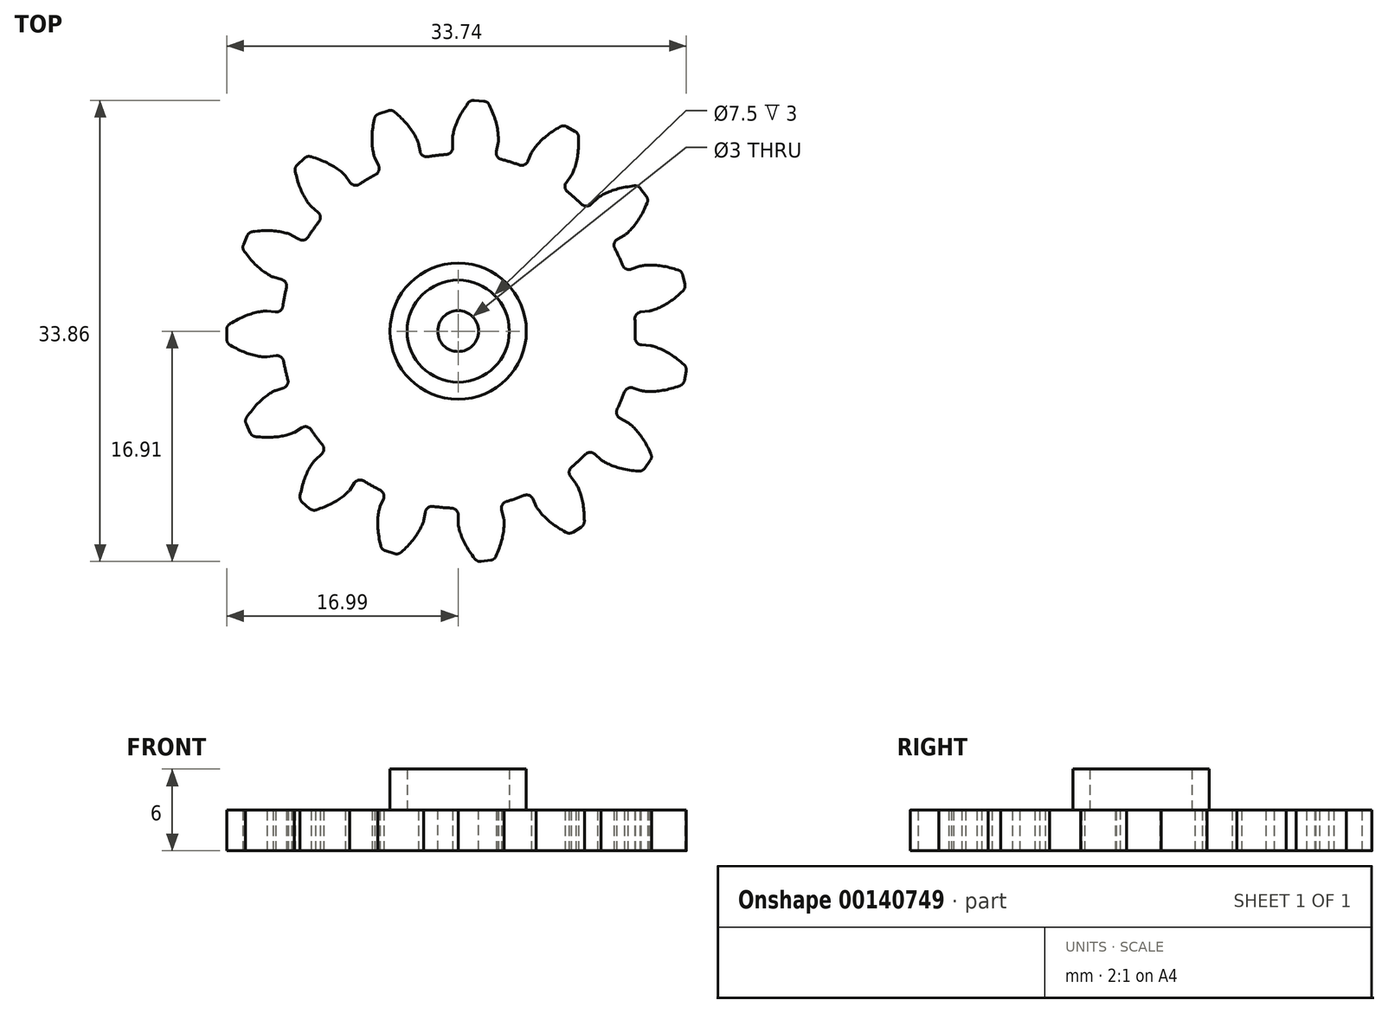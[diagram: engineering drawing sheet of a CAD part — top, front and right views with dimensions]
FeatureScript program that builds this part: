
annotation { "Feature Type Name" : "Feature", "Feature Type Description" : "" }
export const myFeature = defineFeature(function(context is Context, id is Id, definition is map)
    precondition{}
    {
        {
            var Q0;
            Q0=qCreatedBy(makeId("Top.planeOp"),FACE);
            var sketch = newSketch(context, id + "F0", { "sketchPlane" : qUnion([Q0])});
            skCircle(sketch, "E0", {"center": v(0, 0) * mm, "radius": 13 * mm});
            skCircle(sketch, "E1", {"center": v(0, 0) * mm, "radius": 15 * mm, "construction": true});
            skCircle(sketch, "E2", {"center": v(0, 0) * mm, "radius": 17 * mm, "construction": true});
            skLineSegment(sketch, "E3", {"start": v(0, 0) * mm, "end": v(0, 22.2) * mm, "construction": true});
            skLineSegment(sketch, "E4", {"start": v(0, 0) * mm, "end": v(9.27, 25.47) * mm, "construction": true});
            skLineSegment(sketch, "E5", {"start": v(0, 15) * mm, "end": v(-14.07, 15) * mm, "construction": true});
            skLineSegment(sketch, "E6", {"start": v(0, 15) * mm, "end": v(31.06, 3.7) * mm, "construction": true});
            skCircle(sketch, "E7", {"center": v(0, 0) * mm, "radius": 14.1 * mm, "construction": true});
            skLineSegment(sketch, "E8", {"start": v(0, 0) * mm, "end": v(0, -20.18) * mm, "construction": true});
            skLineSegment(sketch, "E9", {"start": v(0, 0) * mm, "end": v(3.78, -21.45) * mm, "construction": true});
            skLineSegment(sketch, "E10", {"start": v(0, 0) * mm, "end": v(7.83, -21.51) * mm, "construction": true});
            skLineSegment(sketch, "E11", {"start": v(0, 0) * mm, "end": v(12.8, -22.18) * mm, "construction": true});
            skLineSegment(sketch, "E12", {"start": v(0, -14.1) * mm, "end": v(0, -14.1) * mm});
            skLineSegment(sketch, "E13", {"start": v(2.45, -13.88) * mm, "end": v(0.03, -14.3) * mm, "construction": true});
            skLineSegment(sketch, "E14", {"start": v(4.82, -13.25) * mm, "end": v(0.2, -14.93) * mm, "construction": true});
            skLineSegment(sketch, "E15", {"start": v(7.05, -12.2) * mm, "end": v(0.66, -15.9) * mm, "construction": true});
            skLineSegment(sketch, "E16", {"start": v(0, 0) * mm, "end": v(20.1, -23.94) * mm, "construction": true});
            skLineSegment(sketch, "E17", {"start": v(9.06, -10.8) * mm, "end": v(1.52, -17.12) * mm, "construction": true});
            skFitSpline(sketch, "E18", {"points": [v(0, -14.1) * mm, v(0.03, -14.3) * mm, v(0.2, -14.93) * mm, v(0.66, -15.9) * mm, v(1.52, -17.12) * mm], "startDerivative": vector(0.1, -1.43) * mm, "endDerivative": vector(2.7, -3.57) * mm});
            skLineSegment(sketch, "E19", {"start": v(0, 0) * mm, "end": v(2.4, -19.98) * mm, "construction": true});
            skLineSegment(sketch, "E20", {"start": v(0.22, -15) * mm, "end": v(0, 0) * mm, "construction": true});
            skFitSpline(sketch, "E21.MirrorCS", {"points": [v(3.34, -13.7) * mm, v(3.37, -13.9) * mm, v(3.34, -14.55) * mm, v(3.13, -15.6) * mm, v(2.58, -17) * mm], "startDerivative": vector(0.24, -1.41) * mm, "endDerivative": vector(-1.78, -4.11) * mm});
            skLineSegment(sketch, "E22", {"start": v(1.39, -16.94) * mm, "end": v(2.67, -16.79) * mm});
            skLineSegment(sketch, "E23", {"start": v(0, -14.1) * mm, "end": v(0, -13) * mm});
            skLineSegment(sketch, "E24", {"start": v(3.35, -13.76) * mm, "end": v(0, 0) * mm});
            skSolve(sketch);
        }
        {
            var Q0;
            Q0 = qSketchRegion(id + "F0", true);
            extrude(context, id + "F1", {"entities" : qUnion([Q0]), "depth" : 3 * mm});
        }
        {
            var Q0;
            Q0=qCreatedBy(makeId("Front.planeOp"),FACE);
            var sketch = newSketch(context, id + "F2", { "sketchPlane" : qUnion([Q0])});
            skLineSegment(sketch, "E25", {"start": v(0, 0) * mm, "end": v(0, 54.12) * mm, "construction": true});
            skSolve(sketch);
        }
        {
            var Q0;
            Q0=makeQuery(id+"F1.opExtrude","SWEPT_EDGE",EDGE,{"disambiguationData":[OSD([sQuery(id+"F0.wireOp",EDGE,"E0"),sQuery(id+"F0.wireOp",EDGE,"E24")])]});
            var Q1;
            Q1=makeQuery(id+"F1.opExtrude","SWEPT_EDGE",EDGE,{"disambiguationData":[OSD([sQuery(id+"F0.wireOp",EDGE,"E0"),sQuery(id+"F0.wireOp",EDGE,"E23")])]});
            fillet(context, id + "F3", {"entities" : qUnion([Q0, Q1]), "radius" : .5 * mm, "tangentPropagation" : true, "allowEdgeOverflow" : false});
        }
        {
            var Q0;
            Q0=makeQuery(id+"F1.opExtrude","SWEPT_EDGE",EDGE,{"disambiguationData":[OSD([sQuery(id+"F0.wireOp",EDGE,"E18"),sQuery(id+"F0.wireOp",EDGE,"E22")])]});
            var Q1;
            Q1=makeQuery(id+"F1.opExtrude","SWEPT_EDGE",EDGE,{"disambiguationData":[OSD([sQuery(id+"F0.wireOp",EDGE,"E21.MirrorCS"),sQuery(id+"F0.wireOp",EDGE,"E22")])]});
            fillet(context, id + "F4", {"entities" : qUnion([Q0, Q1]), "radius" : .5 * mm, "tangentPropagation" : true, "allowEdgeOverflow" : false});
        }
        {
            var Q0;
            Q0=makeQuery(id+"F1.opExtrude","SWEPT_BODY",BODY,{"disambiguationData":[OSD([sQuery(id+"F0.wireOp",EDGE,"E0"),sQuery(id+"F0.wireOp",EDGE,"E18"),sQuery(id+"F0.wireOp",EDGE,"E21.MirrorCS"),sQuery(id+"F0.wireOp",EDGE,"E22"),sQuery(id+"F0.wireOp",EDGE,"E23"),sQuery(id+"F0.wireOp",EDGE,"E24")])]});
            var Q1;
            Q1=sQuery(id+"F2.wireOp",EDGE,"E25");
            circularPattern(context, id + "F5", {"operationType" : NewBodyOperationType.ADD, "entities" : qUnion([Q0]), "axis" : qUnion([Q1]), "angle" : 24 * degree, "instanceCount" : 15});
        }
        {
            var Q0;
            {var subQ0=makeQuery(id+"F1.opExtrude","CAP_FACE",FACE,{"disambiguationData":[OSD([sQuery(id+"F0.wireOp",EDGE,"E0"),sQuery(id+"F0.wireOp",EDGE,"E18"),sQuery(id+"F0.wireOp",EDGE,"E21.MirrorCS"),sQuery(id+"F0.wireOp",EDGE,"E22"),sQuery(id+"F0.wireOp",EDGE,"E23"),sQuery(id+"F0.wireOp",EDGE,"E24")])],"isStart":false});Q0=makeQuery(id+"F5.boolean.opBoolean","MERGE",FACE,{"derivedFrom":[subQ0,makeQuery(id+"F5.opPattern","COPY",FACE,{"derivedFrom":subQ0,"instanceName":"1"}),makeQuery(id+"F5.opPattern","COPY",FACE,{"derivedFrom":subQ0,"instanceName":"2"}),makeQuery(id+"F5.opPattern","COPY",FACE,{"derivedFrom":subQ0,"instanceName":"3"}),makeQuery(id+"F5.opPattern","COPY",FACE,{"derivedFrom":subQ0,"instanceName":"4"}),makeQuery(id+"F5.opPattern","COPY",FACE,{"derivedFrom":subQ0,"instanceName":"5"}),makeQuery(id+"F5.opPattern","COPY",FACE,{"derivedFrom":subQ0,"instanceName":"6"}),makeQuery(id+"F5.opPattern","COPY",FACE,{"derivedFrom":subQ0,"instanceName":"7"}),makeQuery(id+"F5.opPattern","COPY",FACE,{"derivedFrom":subQ0,"instanceName":"8"}),makeQuery(id+"F5.opPattern","COPY",FACE,{"derivedFrom":subQ0,"instanceName":"9"}),makeQuery(id+"F5.opPattern","COPY",FACE,{"derivedFrom":subQ0,"instanceName":"10"}),makeQuery(id+"F5.opPattern","COPY",FACE,{"derivedFrom":subQ0,"instanceName":"11"}),makeQuery(id+"F5.opPattern","COPY",FACE,{"derivedFrom":subQ0,"instanceName":"12"}),makeQuery(id+"F5.opPattern","COPY",FACE,{"derivedFrom":subQ0,"instanceName":"13"}),makeQuery(id+"F5.opPattern","COPY",FACE,{"derivedFrom":subQ0,"instanceName":"14"})]});}
            var sketch = newSketch(context, id + "F6", { "sketchPlane" : qUnion([Q0])});
            skCircle(sketch, "E26", {"center": v(0, 0) * mm, "radius": 1.5 * mm});
            skCircle(sketch, "E27", {"center": v(0, 0) * mm, "radius": 3.75 * mm});
            skCircle(sketch, "E28", {"center": v(0, 0) * mm, "radius": 5 * mm});
            skSolve(sketch);
        }
        {
            var Q0;
            Q0=makeQuery(id+"F6.imprint","IMPRINT",FACE,{"disambiguationData":[TD([[makeQuery(id+"F6.imprint","IMPRINT",EDGE,{"derivedFrom":sQuery(id+"F6.wireOp",EDGE,"E27")}),-1.0]])]});
            extrude(context, id + "F7", {"entities" : qUnion([Q0]), "operationType" : NewBodyOperationType.ADD, "depth" : 3 * mm});
        }
        {
            var Q0;
            Q0=makeQuery(id+"F6.imprint","IMPRINT",FACE,{"disambiguationData":[TD([[makeQuery(id+"F6.imprint","IMPRINT",EDGE,{"derivedFrom":sQuery(id+"F6.wireOp",EDGE,"E26")}),1.0]])]});
            extrude(context, id + "F8", {"entities" : qUnion([Q0]), "operationType" : NewBodyOperationType.REMOVE, "oppositeDirection" : true, "depth" : 25 * mm});
        }
    });
